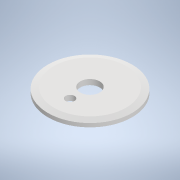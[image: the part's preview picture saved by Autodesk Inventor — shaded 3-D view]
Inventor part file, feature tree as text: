
AUTODESK INVENTOR PART (.ipt)
format: ipt  version: 2021 (Build 250183000, 183)  size: 135,680 bytes
history: native  units: mm
features: sketch x2, revolve x1, extrude x1
ambient origin geometry x8: Origin, YZ Plane, XZ Plane, XY Plane, X Axis, Y Axis, Z Axis, Center Point
bodies: Solid1 (feature_tree)
feature tree (4):
  revolve  "Revolution1"  [1 undecoded]
  extrude  "Extrusion1"  Depth=3.5mm
  sketch  "Sketch1"  dims[d0=95.0mm d1=12.0mm]
  sketch  "Sketch2"  dims[d2=8.4mm d3=3.5mm d4=3.0mm d5=73.5mm d6=165.0deg d7=90.0deg d8=44.0mm d9=20.0mm d10=60.0mm d11=0.0mm d12=0.0mm]
note: 1 required parameter value undecoded (feature->parameter linkage not recoverable at this tier; creation-order binding heuristic only, values carry confidence <= 0.55)
